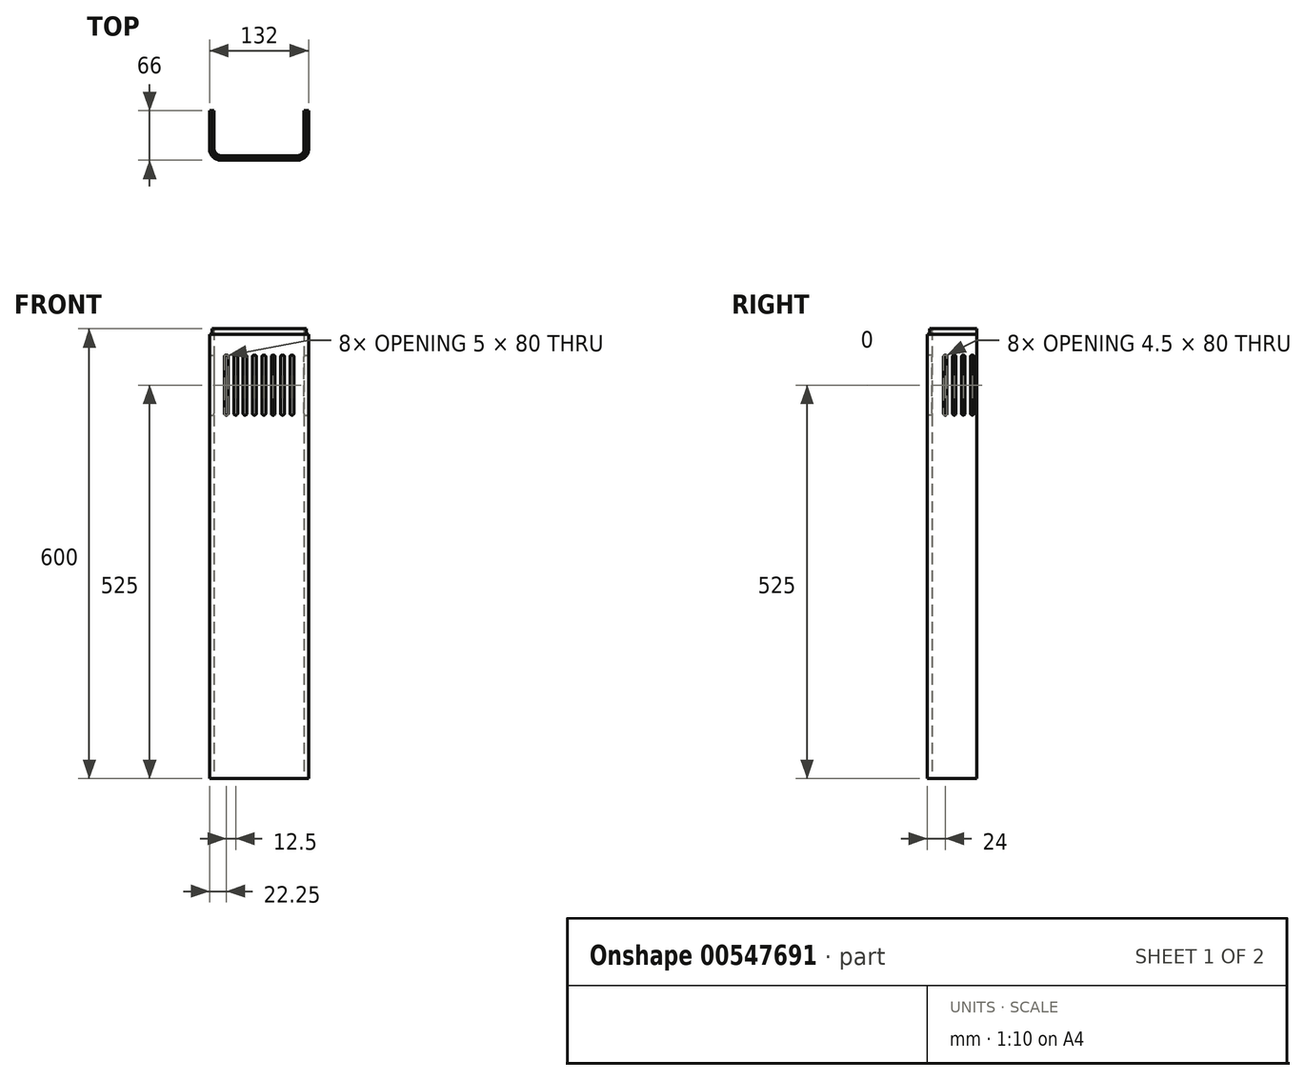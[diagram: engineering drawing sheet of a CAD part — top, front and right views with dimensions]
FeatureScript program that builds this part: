
annotation { "Feature Type Name" : "Feature", "Feature Type Description" : "" }
export const myFeature = defineFeature(function(context is Context, id is Id, definition is map)
    precondition{}
    {
        {
            var Q0;
            Q0=qCreatedBy(makeId("Top.planeOp"),FACE);
            var sketch = newSketch(context, id + "F0", { "sketchPlane" : qUnion([Q0])});
            skLineSegment(sketch, "E0", {"start": v(-66, 0) * mm, "end": v(-66, -51) * mm});
            skLineSegment(sketch, "E1", {"start": v(-51, -66) * mm, "end": v(51, -66) * mm});
            skLineSegment(sketch, "E2", {"start": v(66, -51) * mm, "end": v(66, 0) * mm});
            skPoint(sketch, "E3", {"position": v(0, -66) * mm});
            skPoint(sketch, "E4.visualSharp", {"position": v(-66, -66) * mm});
            skArc(sketch, "E4.filletArc", {"start": v(-66, -51) * mm, "mid": v(-61.6, -61.6) * mm, "end": v(-51, -66) * mm});
            skPoint(sketch, "E5.visualSharp", {"position": v(66, -66) * mm});
            skArc(sketch, "E5.filletArc", {"start": v(51, -66) * mm, "mid": v(61.6, -61.6) * mm, "end": v(66, -51) * mm});
            skLineSegment(sketch, "E6.0", {"start": v(-60, 0) * mm, "end": v(-60, -51) * mm});
            skArc(sketch, "E7.0", {"start": v(-60, -51) * mm, "mid": v(-57.36, -57.36) * mm, "end": v(-51, -60) * mm});
            skLineSegment(sketch, "E8.0", {"start": v(60, -51) * mm, "end": v(60, 0) * mm});
            skArc(sketch, "E8.1", {"start": v(51, -60) * mm, "mid": v(57.36, -57.36) * mm, "end": v(60, -51) * mm});
            skLineSegment(sketch, "E8.2", {"start": v(-51, -60) * mm, "end": v(51, -60) * mm});
            skLineSegment(sketch, "E9", {"start": v(-66, 0) * mm, "end": v(-60, 0) * mm});
            skLineSegment(sketch, "E10", {"start": v(60, 0) * mm, "end": v(66, 0) * mm});
            skSolve(sketch);
        }
        {
            var Q0;
            Q0 = qSketchRegion(id + "F0", true);
            extrude(context, id + "F1", {"entities" : qUnion([Q0]), "depth" : 600 * mm, "offsetDistance" : 25 * mm});
        }
        {
            var Q0;
            Q0=makeQuery(id+"F1.opExtrude","SWEPT_FACE",FACE,{"disambiguationData":[OSD([sQuery(id+"F0.wireOp",EDGE,"E1")])]});
            var sketch = newSketch(context, id + "F2", { "sketchPlane" : qUnion([Q0])});
            skLineSegment(sketch, "E11.bottom", {"start": v(-46.25, 565) * mm, "end": v(-41.25, 565) * mm});
            skLineSegment(sketch, "E11.top", {"start": v(-46.25, 485) * mm, "end": v(-41.25, 485) * mm});
            skLineSegment(sketch, "E11.left", {"start": v(-46.25, 565) * mm, "end": v(-46.25, 485) * mm});
            skLineSegment(sketch, "E11.right", {"start": v(-41.25, 565) * mm, "end": v(-41.25, 485) * mm});
            skLineSegment(sketch, "E12", {"start": v(-41.25, 565) * mm, "end": v(-33.75, 565) * mm, "construction": true});
            skPoint(sketch, "E13", {"position": v(0, 600) * mm});
            skLineSegment(sketch, "E14.bottom", {"start": v(-33.75, 565) * mm, "end": v(-28.75, 565) * mm});
            skLineSegment(sketch, "E14.top", {"start": v(-33.75, 485) * mm, "end": v(-28.75, 485) * mm});
            skLineSegment(sketch, "E14.left", {"start": v(-33.75, 565) * mm, "end": v(-33.75, 485) * mm});
            skLineSegment(sketch, "E14.right", {"start": v(-28.75, 565) * mm, "end": v(-28.75, 485) * mm});
            skLineSegment(sketch, "E15.bottom", {"start": v(-21.25, 565) * mm, "end": v(-16.25, 565) * mm});
            skLineSegment(sketch, "E15.top", {"start": v(-21.25, 485) * mm, "end": v(-16.25, 485) * mm});
            skLineSegment(sketch, "E15.left", {"start": v(-21.25, 565) * mm, "end": v(-21.25, 485) * mm});
            skLineSegment(sketch, "E15.right", {"start": v(-16.25, 565) * mm, "end": v(-16.25, 485) * mm});
            skLineSegment(sketch, "E16.bottom", {"start": v(-8.75, 565) * mm, "end": v(-3.75, 565) * mm});
            skLineSegment(sketch, "E16.top", {"start": v(-8.75, 485) * mm, "end": v(-3.75, 485) * mm});
            skLineSegment(sketch, "E16.left", {"start": v(-8.75, 565) * mm, "end": v(-8.75, 485) * mm});
            skLineSegment(sketch, "E16.right", {"start": v(-3.75, 565) * mm, "end": v(-3.75, 485) * mm});
            skLineSegment(sketch, "E17.bottom", {"start": v(3.75, 565) * mm, "end": v(8.75, 565) * mm});
            skLineSegment(sketch, "E17.top", {"start": v(3.75, 485) * mm, "end": v(8.75, 485) * mm});
            skLineSegment(sketch, "E17.left", {"start": v(3.75, 565) * mm, "end": v(3.75, 485) * mm});
            skLineSegment(sketch, "E17.right", {"start": v(8.75, 565) * mm, "end": v(8.75, 485) * mm});
            skLineSegment(sketch, "E18.bottom", {"start": v(16.25, 565) * mm, "end": v(21.25, 565) * mm});
            skLineSegment(sketch, "E18.top", {"start": v(16.25, 485) * mm, "end": v(21.25, 485) * mm});
            skLineSegment(sketch, "E18.left", {"start": v(16.25, 565) * mm, "end": v(16.25, 485) * mm});
            skLineSegment(sketch, "E18.right", {"start": v(21.25, 565) * mm, "end": v(21.25, 485) * mm});
            skLineSegment(sketch, "E19.bottom", {"start": v(28.75, 565) * mm, "end": v(33.75, 565) * mm});
            skLineSegment(sketch, "E19.top", {"start": v(28.75, 485) * mm, "end": v(33.75, 485) * mm});
            skLineSegment(sketch, "E19.left", {"start": v(28.75, 565) * mm, "end": v(28.75, 485) * mm});
            skLineSegment(sketch, "E19.right", {"start": v(33.75, 565) * mm, "end": v(33.75, 485) * mm});
            skLineSegment(sketch, "E20.bottom", {"start": v(41.25, 565) * mm, "end": v(46.25, 565) * mm});
            skLineSegment(sketch, "E20.top", {"start": v(41.25, 485) * mm, "end": v(46.25, 485) * mm});
            skLineSegment(sketch, "E20.left", {"start": v(41.25, 565) * mm, "end": v(41.25, 485) * mm});
            skLineSegment(sketch, "E20.right", {"start": v(46.25, 565) * mm, "end": v(46.25, 485) * mm});
            skLineSegment(sketch, "E21", {"start": v(-28.75, 565) * mm, "end": v(-21.25, 565) * mm, "construction": true});
            skLineSegment(sketch, "E22", {"start": v(-16.25, 565) * mm, "end": v(-8.75, 565) * mm, "construction": true});
            skLineSegment(sketch, "E23", {"start": v(-3.75, 565) * mm, "end": v(3.75, 565) * mm, "construction": true});
            skLineSegment(sketch, "E24", {"start": v(8.75, 565) * mm, "end": v(16.25, 565) * mm, "construction": true});
            skLineSegment(sketch, "E25", {"start": v(21.25, 565) * mm, "end": v(28.75, 565) * mm, "construction": true});
            skLineSegment(sketch, "E26", {"start": v(33.75, 565) * mm, "end": v(41.25, 565) * mm, "construction": true});
            skPoint(sketch, "E27", {"position": v(0, 565) * mm});
            skSolve(sketch);
        }
        {
            var Q0;
            Q0=makeQuery(id+"F2.imprint","IMPRINT",FACE,{"disambiguationData":[TD([[makeQuery(id+"F2.imprint","IMPRINT",EDGE,{"derivedFrom":sQuery(id+"F2.wireOp",EDGE,"E11.bottom")}),-1.0]])]});
            var Q1;
            Q1=makeQuery(id+"F2.imprint","IMPRINT",FACE,{"disambiguationData":[TD([[makeQuery(id+"F2.imprint","IMPRINT",EDGE,{"derivedFrom":sQuery(id+"F2.wireOp",EDGE,"E14.bottom")}),-1.0]])]});
            var Q2;
            Q2=makeQuery(id+"F2.imprint","IMPRINT",FACE,{"disambiguationData":[TD([[makeQuery(id+"F2.imprint","IMPRINT",EDGE,{"derivedFrom":sQuery(id+"F2.wireOp",EDGE,"E15.bottom")}),-1.0]])]});
            var Q3;
            Q3=makeQuery(id+"F2.imprint","IMPRINT",FACE,{"disambiguationData":[TD([[makeQuery(id+"F2.imprint","IMPRINT",EDGE,{"derivedFrom":sQuery(id+"F2.wireOp",EDGE,"E16.bottom")}),-1.0]])]});
            var Q4;
            Q4=makeQuery(id+"F2.imprint","IMPRINT",FACE,{"disambiguationData":[TD([[makeQuery(id+"F2.imprint","IMPRINT",EDGE,{"derivedFrom":sQuery(id+"F2.wireOp",EDGE,"E17.bottom")}),-1.0]])]});
            var Q5;
            Q5=makeQuery(id+"F2.imprint","IMPRINT",FACE,{"disambiguationData":[TD([[makeQuery(id+"F2.imprint","IMPRINT",EDGE,{"derivedFrom":sQuery(id+"F2.wireOp",EDGE,"E18.bottom")}),-1.0]])]});
            var Q6;
            Q6=makeQuery(id+"F2.imprint","IMPRINT",FACE,{"disambiguationData":[TD([[makeQuery(id+"F2.imprint","IMPRINT",EDGE,{"derivedFrom":sQuery(id+"F2.wireOp",EDGE,"E19.bottom")}),-1.0]])]});
            var Q7;
            Q7=makeQuery(id+"F2.imprint","IMPRINT",FACE,{"disambiguationData":[TD([[makeQuery(id+"F2.imprint","IMPRINT",EDGE,{"derivedFrom":sQuery(id+"F2.wireOp",EDGE,"E20.bottom")}),-1.0]])]});
            extrude(context, id + "F3", {"entities" : qUnion([Q0, Q1, Q2, Q3, Q4, Q5, Q6, Q7]), "operationType" : NewBodyOperationType.REMOVE, "oppositeDirection" : true, "depth" : 25 * mm, "offsetDistance" : 25 * mm});
        }
        {
            var Q0;
            Q0=makeQuery(id+"F3.boolean.opBoolean","COPY",EDGE,{"derivedFrom":makeQuery(id+"F3.opExtrude","SWEPT_EDGE",EDGE,{"disambiguationData":[OSD([sQuery(id+"F2.wireOp",EDGE,"E11.top"),sQuery(id+"F2.wireOp",EDGE,"E11.left")])]})});
            var Q1;
            Q1=makeQuery(id+"F3.boolean.opBoolean","COPY",EDGE,{"derivedFrom":makeQuery(id+"F3.opExtrude","SWEPT_EDGE",EDGE,{"disambiguationData":[OSD([sQuery(id+"F2.wireOp",EDGE,"E14.top"),sQuery(id+"F2.wireOp",EDGE,"E14.left")])]})});
            var Q2;
            Q2=makeQuery(id+"F3.boolean.opBoolean","COPY",EDGE,{"derivedFrom":makeQuery(id+"F3.opExtrude","SWEPT_EDGE",EDGE,{"disambiguationData":[OSD([sQuery(id+"F2.wireOp",EDGE,"E15.top"),sQuery(id+"F2.wireOp",EDGE,"E15.left")])]})});
            var Q3;
            Q3=makeQuery(id+"F3.boolean.opBoolean","COPY",EDGE,{"derivedFrom":makeQuery(id+"F3.opExtrude","SWEPT_EDGE",EDGE,{"disambiguationData":[OSD([sQuery(id+"F2.wireOp",EDGE,"E16.top"),sQuery(id+"F2.wireOp",EDGE,"E16.left")])]})});
            var Q4;
            Q4=makeQuery(id+"F3.boolean.opBoolean","COPY",EDGE,{"derivedFrom":makeQuery(id+"F3.opExtrude","SWEPT_EDGE",EDGE,{"disambiguationData":[OSD([sQuery(id+"F2.wireOp",EDGE,"E17.top"),sQuery(id+"F2.wireOp",EDGE,"E17.left")])]})});
            var Q5;
            Q5=makeQuery(id+"F3.boolean.opBoolean","COPY",EDGE,{"derivedFrom":makeQuery(id+"F3.opExtrude","SWEPT_EDGE",EDGE,{"disambiguationData":[OSD([sQuery(id+"F2.wireOp",EDGE,"E18.top"),sQuery(id+"F2.wireOp",EDGE,"E18.left")])]})});
            var Q6;
            Q6=makeQuery(id+"F3.boolean.opBoolean","COPY",EDGE,{"derivedFrom":makeQuery(id+"F3.opExtrude","SWEPT_EDGE",EDGE,{"disambiguationData":[OSD([sQuery(id+"F2.wireOp",EDGE,"E19.top"),sQuery(id+"F2.wireOp",EDGE,"E19.left")])]})});
            var Q7;
            Q7=makeQuery(id+"F3.boolean.opBoolean","COPY",EDGE,{"derivedFrom":makeQuery(id+"F3.opExtrude","SWEPT_EDGE",EDGE,{"disambiguationData":[OSD([sQuery(id+"F2.wireOp",EDGE,"E20.top"),sQuery(id+"F2.wireOp",EDGE,"E20.left")])]})});
            var Q8;
            Q8=makeQuery(id+"F3.boolean.opBoolean","COPY",EDGE,{"derivedFrom":makeQuery(id+"F3.opExtrude","SWEPT_EDGE",EDGE,{"disambiguationData":[OSD([sQuery(id+"F2.wireOp",EDGE,"E11.bottom"),sQuery(id+"F2.wireOp",EDGE,"E11.left")])]})});
            var Q9;
            Q9=makeQuery(id+"F3.boolean.opBoolean","COPY",EDGE,{"derivedFrom":makeQuery(id+"F3.opExtrude","SWEPT_EDGE",EDGE,{"disambiguationData":[OSD([sQuery(id+"F2.wireOp",EDGE,"E14.bottom"),sQuery(id+"F2.wireOp",EDGE,"E14.left")])]})});
            var Q10;
            Q10=makeQuery(id+"F3.boolean.opBoolean","COPY",EDGE,{"derivedFrom":makeQuery(id+"F3.opExtrude","SWEPT_EDGE",EDGE,{"disambiguationData":[OSD([sQuery(id+"F2.wireOp",EDGE,"E15.bottom"),sQuery(id+"F2.wireOp",EDGE,"E15.left")])]})});
            var Q11;
            Q11=makeQuery(id+"F3.boolean.opBoolean","COPY",EDGE,{"derivedFrom":makeQuery(id+"F3.opExtrude","SWEPT_EDGE",EDGE,{"disambiguationData":[OSD([sQuery(id+"F2.wireOp",EDGE,"E16.bottom"),sQuery(id+"F2.wireOp",EDGE,"E16.left")])]})});
            var Q12;
            Q12=makeQuery(id+"F3.boolean.opBoolean","COPY",EDGE,{"derivedFrom":makeQuery(id+"F3.opExtrude","SWEPT_EDGE",EDGE,{"disambiguationData":[OSD([sQuery(id+"F2.wireOp",EDGE,"E17.bottom"),sQuery(id+"F2.wireOp",EDGE,"E17.left")])]})});
            var Q13;
            Q13=makeQuery(id+"F3.boolean.opBoolean","COPY",EDGE,{"derivedFrom":makeQuery(id+"F3.opExtrude","SWEPT_EDGE",EDGE,{"disambiguationData":[OSD([sQuery(id+"F2.wireOp",EDGE,"E18.bottom"),sQuery(id+"F2.wireOp",EDGE,"E18.left")])]})});
            var Q14;
            Q14=makeQuery(id+"F3.boolean.opBoolean","COPY",EDGE,{"derivedFrom":makeQuery(id+"F3.opExtrude","SWEPT_EDGE",EDGE,{"disambiguationData":[OSD([sQuery(id+"F2.wireOp",EDGE,"E19.bottom"),sQuery(id+"F2.wireOp",EDGE,"E19.left")])]})});
            var Q15;
            Q15=makeQuery(id+"F3.boolean.opBoolean","COPY",EDGE,{"derivedFrom":makeQuery(id+"F3.opExtrude","SWEPT_EDGE",EDGE,{"disambiguationData":[OSD([sQuery(id+"F2.wireOp",EDGE,"E20.bottom"),sQuery(id+"F2.wireOp",EDGE,"E20.left")])]})});
            var Q16;
            Q16=makeQuery(id+"F3.boolean.opBoolean","COPY",EDGE,{"derivedFrom":makeQuery(id+"F3.opExtrude","SWEPT_EDGE",EDGE,{"disambiguationData":[OSD([sQuery(id+"F2.wireOp",EDGE,"E11.bottom"),sQuery(id+"F2.wireOp",EDGE,"E11.right")])]})});
            var Q17;
            Q17=makeQuery(id+"F3.boolean.opBoolean","COPY",EDGE,{"derivedFrom":makeQuery(id+"F3.opExtrude","SWEPT_EDGE",EDGE,{"disambiguationData":[OSD([sQuery(id+"F2.wireOp",EDGE,"E14.bottom"),sQuery(id+"F2.wireOp",EDGE,"E14.right")])]})});
            var Q18;
            Q18=makeQuery(id+"F3.boolean.opBoolean","COPY",EDGE,{"derivedFrom":makeQuery(id+"F3.opExtrude","SWEPT_EDGE",EDGE,{"disambiguationData":[OSD([sQuery(id+"F2.wireOp",EDGE,"E15.bottom"),sQuery(id+"F2.wireOp",EDGE,"E15.right")])]})});
            var Q19;
            Q19=makeQuery(id+"F3.boolean.opBoolean","COPY",EDGE,{"derivedFrom":makeQuery(id+"F3.opExtrude","SWEPT_EDGE",EDGE,{"disambiguationData":[OSD([sQuery(id+"F2.wireOp",EDGE,"E16.bottom"),sQuery(id+"F2.wireOp",EDGE,"E16.right")])]})});
            var Q20;
            Q20=makeQuery(id+"F3.boolean.opBoolean","COPY",EDGE,{"derivedFrom":makeQuery(id+"F3.opExtrude","SWEPT_EDGE",EDGE,{"disambiguationData":[OSD([sQuery(id+"F2.wireOp",EDGE,"E17.bottom"),sQuery(id+"F2.wireOp",EDGE,"E17.right")])]})});
            var Q21;
            Q21=makeQuery(id+"F3.boolean.opBoolean","COPY",EDGE,{"derivedFrom":makeQuery(id+"F3.opExtrude","SWEPT_EDGE",EDGE,{"disambiguationData":[OSD([sQuery(id+"F2.wireOp",EDGE,"E18.bottom"),sQuery(id+"F2.wireOp",EDGE,"E18.right")])]})});
            var Q22;
            Q22=makeQuery(id+"F3.boolean.opBoolean","COPY",EDGE,{"derivedFrom":makeQuery(id+"F3.opExtrude","SWEPT_EDGE",EDGE,{"disambiguationData":[OSD([sQuery(id+"F2.wireOp",EDGE,"E19.bottom"),sQuery(id+"F2.wireOp",EDGE,"E19.right")])]})});
            var Q23;
            Q23=makeQuery(id+"F3.boolean.opBoolean","COPY",EDGE,{"derivedFrom":makeQuery(id+"F3.opExtrude","SWEPT_EDGE",EDGE,{"disambiguationData":[OSD([sQuery(id+"F2.wireOp",EDGE,"E20.bottom"),sQuery(id+"F2.wireOp",EDGE,"E20.right")])]})});
            var Q24;
            Q24=makeQuery(id+"F3.boolean.opBoolean","COPY",EDGE,{"derivedFrom":makeQuery(id+"F3.opExtrude","SWEPT_EDGE",EDGE,{"disambiguationData":[OSD([sQuery(id+"F2.wireOp",EDGE,"E20.top"),sQuery(id+"F2.wireOp",EDGE,"E20.right")])]})});
            var Q25;
            Q25=makeQuery(id+"F3.boolean.opBoolean","COPY",EDGE,{"derivedFrom":makeQuery(id+"F3.opExtrude","SWEPT_EDGE",EDGE,{"disambiguationData":[OSD([sQuery(id+"F2.wireOp",EDGE,"E19.top"),sQuery(id+"F2.wireOp",EDGE,"E19.right")])]})});
            var Q26;
            Q26=makeQuery(id+"F3.boolean.opBoolean","COPY",EDGE,{"derivedFrom":makeQuery(id+"F3.opExtrude","SWEPT_EDGE",EDGE,{"disambiguationData":[OSD([sQuery(id+"F2.wireOp",EDGE,"E18.top"),sQuery(id+"F2.wireOp",EDGE,"E18.right")])]})});
            var Q27;
            Q27=makeQuery(id+"F3.boolean.opBoolean","COPY",EDGE,{"derivedFrom":makeQuery(id+"F3.opExtrude","SWEPT_EDGE",EDGE,{"disambiguationData":[OSD([sQuery(id+"F2.wireOp",EDGE,"E17.top"),sQuery(id+"F2.wireOp",EDGE,"E17.right")])]})});
            var Q28;
            Q28=makeQuery(id+"F3.boolean.opBoolean","COPY",EDGE,{"derivedFrom":makeQuery(id+"F3.opExtrude","SWEPT_EDGE",EDGE,{"disambiguationData":[OSD([sQuery(id+"F2.wireOp",EDGE,"E16.top"),sQuery(id+"F2.wireOp",EDGE,"E16.right")])]})});
            var Q29;
            Q29=makeQuery(id+"F3.boolean.opBoolean","COPY",EDGE,{"derivedFrom":makeQuery(id+"F3.opExtrude","SWEPT_EDGE",EDGE,{"disambiguationData":[OSD([sQuery(id+"F2.wireOp",EDGE,"E15.top"),sQuery(id+"F2.wireOp",EDGE,"E15.right")])]})});
            var Q30;
            Q30=makeQuery(id+"F3.boolean.opBoolean","COPY",EDGE,{"derivedFrom":makeQuery(id+"F3.opExtrude","SWEPT_EDGE",EDGE,{"disambiguationData":[OSD([sQuery(id+"F2.wireOp",EDGE,"E14.top"),sQuery(id+"F2.wireOp",EDGE,"E14.right")])]})});
            var Q31;
            Q31=makeQuery(id+"F3.boolean.opBoolean","COPY",EDGE,{"derivedFrom":makeQuery(id+"F3.opExtrude","SWEPT_EDGE",EDGE,{"disambiguationData":[OSD([sQuery(id+"F2.wireOp",EDGE,"E11.top"),sQuery(id+"F2.wireOp",EDGE,"E11.right")])]})});
            fillet(context, id + "F4", {"entities" : qUnion([Q0, Q1, Q2, Q3, Q4, Q5, Q6, Q7, Q8, Q9, Q10, Q11, Q12, Q13, Q14, Q15, Q16, Q17, Q18, Q19, Q20, Q21, Q22, Q23, Q24, Q25, Q26, Q27, Q28, Q29, Q30, Q31]), "radius" : 2 * mm, "tangentPropagation" : true, "allowEdgeOverflow" : false});
        }
        {
            var Q0;
            Q0=makeQuery(id+"F1.opExtrude","SWEPT_FACE",FACE,{"disambiguationData":[OSD([sQuery(id+"F0.wireOp",EDGE,"E2")])]});
            var sketch = newSketch(context, id + "F5", { "sketchPlane" : qUnion([Q0])});
            skLineSegment(sketch, "E28.bottom", {"start": v(-44.25, 485) * mm, "end": v(-39.75, 485) * mm});
            skLineSegment(sketch, "E28.top", {"start": v(-44.25, 565) * mm, "end": v(-39.75, 565) * mm});
            skLineSegment(sketch, "E28.left", {"start": v(-44.25, 485) * mm, "end": v(-44.25, 565) * mm});
            skLineSegment(sketch, "E28.right", {"start": v(-39.75, 485) * mm, "end": v(-39.75, 565) * mm});
            skLineSegment(sketch, "E29.bottom", {"start": v(-32.25, 565) * mm, "end": v(-27.75, 565) * mm});
            skLineSegment(sketch, "E29.top", {"start": v(-32.25, 485) * mm, "end": v(-27.75, 485) * mm});
            skLineSegment(sketch, "E29.left", {"start": v(-32.25, 565) * mm, "end": v(-32.25, 485) * mm});
            skLineSegment(sketch, "E29.right", {"start": v(-27.75, 565) * mm, "end": v(-27.75, 485) * mm});
            skLineSegment(sketch, "E30.bottom", {"start": v(-20.25, 565) * mm, "end": v(-15.75, 565) * mm});
            skLineSegment(sketch, "E30.top", {"start": v(-20.25, 485) * mm, "end": v(-15.75, 485) * mm});
            skLineSegment(sketch, "E30.left", {"start": v(-20.25, 565) * mm, "end": v(-20.25, 485) * mm});
            skLineSegment(sketch, "E30.right", {"start": v(-15.75, 565) * mm, "end": v(-15.75, 485) * mm});
            skLineSegment(sketch, "E31.bottom", {"start": v(-8.25, 565) * mm, "end": v(-3.75, 565) * mm});
            skLineSegment(sketch, "E31.top", {"start": v(-8.25, 485) * mm, "end": v(-3.75, 485) * mm});
            skLineSegment(sketch, "E31.left", {"start": v(-8.25, 565) * mm, "end": v(-8.25, 485) * mm});
            skLineSegment(sketch, "E31.right", {"start": v(-3.75, 565) * mm, "end": v(-3.75, 485) * mm});
            skLineSegment(sketch, "E32", {"start": v(-39.75, 565) * mm, "end": v(-32.25, 565) * mm, "construction": true});
            skLineSegment(sketch, "E33", {"start": v(-27.75, 565) * mm, "end": v(-20.25, 565) * mm, "construction": true});
            skLineSegment(sketch, "E34", {"start": v(-15.75, 565) * mm, "end": v(-8.25, 565) * mm, "construction": true});
            skLineSegment(sketch, "E35", {"start": v(-3.75, 565) * mm, "end": v(3.75, 565) * mm, "construction": true});
            skPoint(sketch, "E36", {"position": v(0, 565) * mm});
            skSolve(sketch);
        }
        {
            var Q0;
            Q0=makeQuery(id+"F5.imprint","IMPRINT",FACE,{"disambiguationData":[TD([[makeQuery(id+"F5.imprint","IMPRINT",EDGE,{"derivedFrom":sQuery(id+"F5.wireOp",EDGE,"E28.bottom")}),1.0]])]});
            var Q1;
            Q1=makeQuery(id+"F5.imprint","IMPRINT",FACE,{"disambiguationData":[TD([[makeQuery(id+"F5.imprint","IMPRINT",EDGE,{"derivedFrom":sQuery(id+"F5.wireOp",EDGE,"E29.bottom")}),-1.0]])]});
            var Q2;
            Q2=makeQuery(id+"F5.imprint","IMPRINT",FACE,{"disambiguationData":[TD([[makeQuery(id+"F5.imprint","IMPRINT",EDGE,{"derivedFrom":sQuery(id+"F5.wireOp",EDGE,"E30.bottom")}),-1.0]])]});
            var Q3;
            Q3=makeQuery(id+"F5.imprint","IMPRINT",FACE,{"disambiguationData":[TD([[makeQuery(id+"F5.imprint","IMPRINT",EDGE,{"derivedFrom":sQuery(id+"F5.wireOp",EDGE,"E31.bottom")}),-1.0]])]});
            extrude(context, id + "F6", {"entities" : qUnion([Q0, Q1, Q2, Q3]), "operationType" : NewBodyOperationType.REMOVE, "endBound" : BoundingType.THROUGH_ALL, "oppositeDirection" : true, "depth" : 25 * mm, "offsetDistance" : 25 * mm});
        }
        {
            var Q0;
            {var subQ0=sQuery(id+"F5.wireOp",EDGE,"E31.top");var subQ1=sQuery(id+"F5.wireOp",EDGE,"E31.right");Q0=makeQuery(id+"F6.boolean.opBoolean","COPY",EDGE,{"disambiguationData":[TD([makeQuery(id+"F1.opExtrude","SWEPT_FACE",FACE,{"disambiguationData":[OSD([sQuery(id+"F0.wireOp",EDGE,"E2")])]})])],"derivedFrom":makeQuery(id+"F6.opExtrude","SWEPT_EDGE",EDGE,{"disambiguationData":[OSD([subQ0,subQ1])]})});}
            var Q1;
            {var subQ0=sQuery(id+"F5.wireOp",EDGE,"E30.top");var subQ1=sQuery(id+"F5.wireOp",EDGE,"E30.right");Q1=makeQuery(id+"F6.boolean.opBoolean","COPY",EDGE,{"disambiguationData":[TD([makeQuery(id+"F1.opExtrude","SWEPT_FACE",FACE,{"disambiguationData":[OSD([sQuery(id+"F0.wireOp",EDGE,"E2")])]})])],"derivedFrom":makeQuery(id+"F6.opExtrude","SWEPT_EDGE",EDGE,{"disambiguationData":[OSD([subQ0,subQ1])]})});}
            var Q2;
            {var subQ0=sQuery(id+"F5.wireOp",EDGE,"E29.right");var subQ1=sQuery(id+"F5.wireOp",EDGE,"E29.top");Q2=makeQuery(id+"F6.boolean.opBoolean","COPY",EDGE,{"disambiguationData":[TD([makeQuery(id+"F1.opExtrude","SWEPT_FACE",FACE,{"disambiguationData":[OSD([sQuery(id+"F0.wireOp",EDGE,"E2")])]})])],"derivedFrom":makeQuery(id+"F6.opExtrude","SWEPT_EDGE",EDGE,{"disambiguationData":[OSD([subQ1,subQ0])]})});}
            var Q3;
            {var subQ0=sQuery(id+"F5.wireOp",EDGE,"E28.bottom");var subQ1=sQuery(id+"F5.wireOp",EDGE,"E28.right");Q3=makeQuery(id+"F6.boolean.opBoolean","COPY",EDGE,{"disambiguationData":[TD([makeQuery(id+"F1.opExtrude","SWEPT_FACE",FACE,{"disambiguationData":[OSD([sQuery(id+"F0.wireOp",EDGE,"E2")])]})])],"derivedFrom":makeQuery(id+"F6.opExtrude","SWEPT_EDGE",EDGE,{"disambiguationData":[OSD([subQ0,subQ1])]})});}
            var Q4;
            {var subQ0=sQuery(id+"F5.wireOp",EDGE,"E28.bottom");var subQ1=sQuery(id+"F5.wireOp",EDGE,"E28.left");Q4=makeQuery(id+"F6.boolean.opBoolean","COPY",EDGE,{"disambiguationData":[TD([makeQuery(id+"F1.opExtrude","SWEPT_FACE",FACE,{"disambiguationData":[OSD([sQuery(id+"F0.wireOp",EDGE,"E2")])]})])],"derivedFrom":makeQuery(id+"F6.opExtrude","SWEPT_EDGE",EDGE,{"disambiguationData":[OSD([subQ0,subQ1])]})});}
            var Q5;
            {var subQ0=sQuery(id+"F5.wireOp",EDGE,"E29.top");var subQ1=sQuery(id+"F5.wireOp",EDGE,"E29.left");Q5=makeQuery(id+"F6.boolean.opBoolean","COPY",EDGE,{"disambiguationData":[TD([makeQuery(id+"F1.opExtrude","SWEPT_FACE",FACE,{"disambiguationData":[OSD([sQuery(id+"F0.wireOp",EDGE,"E2")])]})])],"derivedFrom":makeQuery(id+"F6.opExtrude","SWEPT_EDGE",EDGE,{"disambiguationData":[OSD([subQ0,subQ1])]})});}
            var Q6;
            {var subQ0=sQuery(id+"F5.wireOp",EDGE,"E30.left");var subQ1=sQuery(id+"F5.wireOp",EDGE,"E30.top");Q6=makeQuery(id+"F6.boolean.opBoolean","COPY",EDGE,{"disambiguationData":[TD([makeQuery(id+"F1.opExtrude","SWEPT_FACE",FACE,{"disambiguationData":[OSD([sQuery(id+"F0.wireOp",EDGE,"E2")])]})])],"derivedFrom":makeQuery(id+"F6.opExtrude","SWEPT_EDGE",EDGE,{"disambiguationData":[OSD([subQ1,subQ0])]})});}
            var Q7;
            {var subQ0=sQuery(id+"F5.wireOp",EDGE,"E31.top");var subQ1=sQuery(id+"F5.wireOp",EDGE,"E31.left");Q7=makeQuery(id+"F6.boolean.opBoolean","COPY",EDGE,{"disambiguationData":[TD([makeQuery(id+"F1.opExtrude","SWEPT_FACE",FACE,{"disambiguationData":[OSD([sQuery(id+"F0.wireOp",EDGE,"E2")])]})])],"derivedFrom":makeQuery(id+"F6.opExtrude","SWEPT_EDGE",EDGE,{"disambiguationData":[OSD([subQ0,subQ1])]})});}
            var Q8;
            {var subQ0=sQuery(id+"F5.wireOp",EDGE,"E28.top");var subQ1=sQuery(id+"F5.wireOp",EDGE,"E28.right");Q8=makeQuery(id+"F6.boolean.opBoolean","COPY",EDGE,{"disambiguationData":[TD([makeQuery(id+"F1.opExtrude","SWEPT_FACE",FACE,{"disambiguationData":[OSD([sQuery(id+"F0.wireOp",EDGE,"E2")])]})])],"derivedFrom":makeQuery(id+"F6.opExtrude","SWEPT_EDGE",EDGE,{"disambiguationData":[OSD([subQ0,subQ1])]})});}
            var Q9;
            {var subQ0=sQuery(id+"F5.wireOp",EDGE,"E29.bottom");var subQ1=sQuery(id+"F5.wireOp",EDGE,"E29.right");Q9=makeQuery(id+"F6.boolean.opBoolean","COPY",EDGE,{"disambiguationData":[TD([makeQuery(id+"F1.opExtrude","SWEPT_FACE",FACE,{"disambiguationData":[OSD([sQuery(id+"F0.wireOp",EDGE,"E2")])]})])],"derivedFrom":makeQuery(id+"F6.opExtrude","SWEPT_EDGE",EDGE,{"disambiguationData":[OSD([subQ0,subQ1])]})});}
            var Q10;
            {var subQ0=sQuery(id+"F5.wireOp",EDGE,"E30.bottom");var subQ1=sQuery(id+"F5.wireOp",EDGE,"E30.right");Q10=makeQuery(id+"F6.boolean.opBoolean","COPY",EDGE,{"disambiguationData":[TD([makeQuery(id+"F1.opExtrude","SWEPT_FACE",FACE,{"disambiguationData":[OSD([sQuery(id+"F0.wireOp",EDGE,"E2")])]})])],"derivedFrom":makeQuery(id+"F6.opExtrude","SWEPT_EDGE",EDGE,{"disambiguationData":[OSD([subQ0,subQ1])]})});}
            var Q11;
            {var subQ0=sQuery(id+"F5.wireOp",EDGE,"E31.bottom");var subQ1=sQuery(id+"F5.wireOp",EDGE,"E31.right");Q11=makeQuery(id+"F6.boolean.opBoolean","COPY",EDGE,{"disambiguationData":[TD([makeQuery(id+"F1.opExtrude","SWEPT_FACE",FACE,{"disambiguationData":[OSD([sQuery(id+"F0.wireOp",EDGE,"E2")])]})])],"derivedFrom":makeQuery(id+"F6.opExtrude","SWEPT_EDGE",EDGE,{"disambiguationData":[OSD([subQ0,subQ1])]})});}
            var Q12;
            {var subQ0=sQuery(id+"F5.wireOp",EDGE,"E31.bottom");var subQ1=sQuery(id+"F5.wireOp",EDGE,"E31.left");Q12=makeQuery(id+"F6.boolean.opBoolean","COPY",EDGE,{"disambiguationData":[TD([makeQuery(id+"F1.opExtrude","SWEPT_FACE",FACE,{"disambiguationData":[OSD([sQuery(id+"F0.wireOp",EDGE,"E2")])]})])],"derivedFrom":makeQuery(id+"F6.opExtrude","SWEPT_EDGE",EDGE,{"disambiguationData":[OSD([subQ0,subQ1])]})});}
            var Q13;
            {var subQ0=sQuery(id+"F5.wireOp",EDGE,"E30.left");var subQ1=sQuery(id+"F5.wireOp",EDGE,"E30.bottom");Q13=makeQuery(id+"F6.boolean.opBoolean","COPY",EDGE,{"disambiguationData":[TD([makeQuery(id+"F1.opExtrude","SWEPT_FACE",FACE,{"disambiguationData":[OSD([sQuery(id+"F0.wireOp",EDGE,"E2")])]})])],"derivedFrom":makeQuery(id+"F6.opExtrude","SWEPT_EDGE",EDGE,{"disambiguationData":[OSD([subQ1,subQ0])]})});}
            var Q14;
            {var subQ0=sQuery(id+"F5.wireOp",EDGE,"E29.bottom");var subQ1=sQuery(id+"F5.wireOp",EDGE,"E29.left");Q14=makeQuery(id+"F6.boolean.opBoolean","COPY",EDGE,{"disambiguationData":[TD([makeQuery(id+"F1.opExtrude","SWEPT_FACE",FACE,{"disambiguationData":[OSD([sQuery(id+"F0.wireOp",EDGE,"E2")])]})])],"derivedFrom":makeQuery(id+"F6.opExtrude","SWEPT_EDGE",EDGE,{"disambiguationData":[OSD([subQ0,subQ1])]})});}
            var Q15;
            {var subQ0=sQuery(id+"F5.wireOp",EDGE,"E28.top");var subQ1=sQuery(id+"F5.wireOp",EDGE,"E28.left");Q15=makeQuery(id+"F6.boolean.opBoolean","COPY",EDGE,{"disambiguationData":[TD([makeQuery(id+"F1.opExtrude","SWEPT_FACE",FACE,{"disambiguationData":[OSD([sQuery(id+"F0.wireOp",EDGE,"E2")])]})])],"derivedFrom":makeQuery(id+"F6.opExtrude","SWEPT_EDGE",EDGE,{"disambiguationData":[OSD([subQ0,subQ1])]})});}
            var Q16;
            {var subQ0=sQuery(id+"F5.wireOp",EDGE,"E28.left");var subQ1=sQuery(id+"F5.wireOp",EDGE,"E28.top");Q16=makeQuery(id+"F6.boolean.opBoolean","COPY",EDGE,{"disambiguationData":[TD([makeQuery(id+"F1.opExtrude","SWEPT_FACE",FACE,{"disambiguationData":[OSD([sQuery(id+"F0.wireOp",EDGE,"E0")])]})])],"derivedFrom":makeQuery(id+"F6.opExtrude","SWEPT_EDGE",EDGE,{"disambiguationData":[OSD([subQ1,subQ0])]})});}
            var Q17;
            {var subQ0=sQuery(id+"F5.wireOp",EDGE,"E29.bottom");var subQ1=sQuery(id+"F5.wireOp",EDGE,"E29.left");Q17=makeQuery(id+"F6.boolean.opBoolean","COPY",EDGE,{"disambiguationData":[TD([makeQuery(id+"F1.opExtrude","SWEPT_FACE",FACE,{"disambiguationData":[OSD([sQuery(id+"F0.wireOp",EDGE,"E0")])]})])],"derivedFrom":makeQuery(id+"F6.opExtrude","SWEPT_EDGE",EDGE,{"disambiguationData":[OSD([subQ0,subQ1])]})});}
            var Q18;
            {var subQ0=sQuery(id+"F5.wireOp",EDGE,"E30.bottom");var subQ1=sQuery(id+"F5.wireOp",EDGE,"E30.left");Q18=makeQuery(id+"F6.boolean.opBoolean","COPY",EDGE,{"disambiguationData":[TD([makeQuery(id+"F1.opExtrude","SWEPT_FACE",FACE,{"disambiguationData":[OSD([sQuery(id+"F0.wireOp",EDGE,"E0")])]})])],"derivedFrom":makeQuery(id+"F6.opExtrude","SWEPT_EDGE",EDGE,{"disambiguationData":[OSD([subQ0,subQ1])]})});}
            var Q19;
            {var subQ0=sQuery(id+"F5.wireOp",EDGE,"E31.left");var subQ1=sQuery(id+"F5.wireOp",EDGE,"E31.bottom");Q19=makeQuery(id+"F6.boolean.opBoolean","COPY",EDGE,{"disambiguationData":[TD([makeQuery(id+"F1.opExtrude","SWEPT_FACE",FACE,{"disambiguationData":[OSD([sQuery(id+"F0.wireOp",EDGE,"E0")])]})])],"derivedFrom":makeQuery(id+"F6.opExtrude","SWEPT_EDGE",EDGE,{"disambiguationData":[OSD([subQ1,subQ0])]})});}
            var Q20;
            {var subQ0=sQuery(id+"F5.wireOp",EDGE,"E28.left");var subQ1=sQuery(id+"F5.wireOp",EDGE,"E28.bottom");Q20=makeQuery(id+"F6.boolean.opBoolean","COPY",EDGE,{"disambiguationData":[TD([makeQuery(id+"F1.opExtrude","SWEPT_FACE",FACE,{"disambiguationData":[OSD([sQuery(id+"F0.wireOp",EDGE,"E0")])]})])],"derivedFrom":makeQuery(id+"F6.opExtrude","SWEPT_EDGE",EDGE,{"disambiguationData":[OSD([subQ1,subQ0])]})});}
            var Q21;
            {var subQ0=sQuery(id+"F5.wireOp",EDGE,"E29.top");var subQ1=sQuery(id+"F5.wireOp",EDGE,"E29.left");Q21=makeQuery(id+"F6.boolean.opBoolean","COPY",EDGE,{"disambiguationData":[TD([makeQuery(id+"F1.opExtrude","SWEPT_FACE",FACE,{"disambiguationData":[OSD([sQuery(id+"F0.wireOp",EDGE,"E0")])]})])],"derivedFrom":makeQuery(id+"F6.opExtrude","SWEPT_EDGE",EDGE,{"disambiguationData":[OSD([subQ0,subQ1])]})});}
            var Q22;
            {var subQ0=sQuery(id+"F5.wireOp",EDGE,"E30.top");var subQ1=sQuery(id+"F5.wireOp",EDGE,"E30.left");Q22=makeQuery(id+"F6.boolean.opBoolean","COPY",EDGE,{"disambiguationData":[TD([makeQuery(id+"F1.opExtrude","SWEPT_FACE",FACE,{"disambiguationData":[OSD([sQuery(id+"F0.wireOp",EDGE,"E0")])]})])],"derivedFrom":makeQuery(id+"F6.opExtrude","SWEPT_EDGE",EDGE,{"disambiguationData":[OSD([subQ0,subQ1])]})});}
            var Q23;
            {var subQ0=sQuery(id+"F5.wireOp",EDGE,"E31.left");var subQ1=sQuery(id+"F5.wireOp",EDGE,"E31.top");Q23=makeQuery(id+"F6.boolean.opBoolean","COPY",EDGE,{"disambiguationData":[TD([makeQuery(id+"F1.opExtrude","SWEPT_FACE",FACE,{"disambiguationData":[OSD([sQuery(id+"F0.wireOp",EDGE,"E0")])]})])],"derivedFrom":makeQuery(id+"F6.opExtrude","SWEPT_EDGE",EDGE,{"disambiguationData":[OSD([subQ1,subQ0])]})});}
            var Q24;
            {var subQ0=sQuery(id+"F5.wireOp",EDGE,"E28.bottom");var subQ1=sQuery(id+"F5.wireOp",EDGE,"E28.right");Q24=makeQuery(id+"F6.boolean.opBoolean","COPY",EDGE,{"disambiguationData":[TD([makeQuery(id+"F1.opExtrude","SWEPT_FACE",FACE,{"disambiguationData":[OSD([sQuery(id+"F0.wireOp",EDGE,"E0")])]})])],"derivedFrom":makeQuery(id+"F6.opExtrude","SWEPT_EDGE",EDGE,{"disambiguationData":[OSD([subQ0,subQ1])]})});}
            var Q25;
            {var subQ0=sQuery(id+"F5.wireOp",EDGE,"E29.top");var subQ1=sQuery(id+"F5.wireOp",EDGE,"E29.right");Q25=makeQuery(id+"F6.boolean.opBoolean","COPY",EDGE,{"disambiguationData":[TD([makeQuery(id+"F1.opExtrude","SWEPT_FACE",FACE,{"disambiguationData":[OSD([sQuery(id+"F0.wireOp",EDGE,"E0")])]})])],"derivedFrom":makeQuery(id+"F6.opExtrude","SWEPT_EDGE",EDGE,{"disambiguationData":[OSD([subQ0,subQ1])]})});}
            var Q26;
            {var subQ0=sQuery(id+"F5.wireOp",EDGE,"E30.right");var subQ1=sQuery(id+"F5.wireOp",EDGE,"E30.top");Q26=makeQuery(id+"F6.boolean.opBoolean","COPY",EDGE,{"disambiguationData":[TD([makeQuery(id+"F1.opExtrude","SWEPT_FACE",FACE,{"disambiguationData":[OSD([sQuery(id+"F0.wireOp",EDGE,"E0")])]})])],"derivedFrom":makeQuery(id+"F6.opExtrude","SWEPT_EDGE",EDGE,{"disambiguationData":[OSD([subQ1,subQ0])]})});}
            var Q27;
            {var subQ0=sQuery(id+"F5.wireOp",EDGE,"E31.top");var subQ1=sQuery(id+"F5.wireOp",EDGE,"E31.right");Q27=makeQuery(id+"F6.boolean.opBoolean","COPY",EDGE,{"disambiguationData":[TD([makeQuery(id+"F1.opExtrude","SWEPT_FACE",FACE,{"disambiguationData":[OSD([sQuery(id+"F0.wireOp",EDGE,"E0")])]})])],"derivedFrom":makeQuery(id+"F6.opExtrude","SWEPT_EDGE",EDGE,{"disambiguationData":[OSD([subQ0,subQ1])]})});}
            var Q28;
            {var subQ0=sQuery(id+"F5.wireOp",EDGE,"E28.top");var subQ1=sQuery(id+"F5.wireOp",EDGE,"E28.right");Q28=makeQuery(id+"F6.boolean.opBoolean","COPY",EDGE,{"disambiguationData":[TD([makeQuery(id+"F1.opExtrude","SWEPT_FACE",FACE,{"disambiguationData":[OSD([sQuery(id+"F0.wireOp",EDGE,"E0")])]})])],"derivedFrom":makeQuery(id+"F6.opExtrude","SWEPT_EDGE",EDGE,{"disambiguationData":[OSD([subQ0,subQ1])]})});}
            var Q29;
            {var subQ0=sQuery(id+"F5.wireOp",EDGE,"E29.bottom");var subQ1=sQuery(id+"F5.wireOp",EDGE,"E29.right");Q29=makeQuery(id+"F6.boolean.opBoolean","COPY",EDGE,{"disambiguationData":[TD([makeQuery(id+"F1.opExtrude","SWEPT_FACE",FACE,{"disambiguationData":[OSD([sQuery(id+"F0.wireOp",EDGE,"E0")])]})])],"derivedFrom":makeQuery(id+"F6.opExtrude","SWEPT_EDGE",EDGE,{"disambiguationData":[OSD([subQ0,subQ1])]})});}
            var Q30;
            {var subQ0=sQuery(id+"F5.wireOp",EDGE,"E30.bottom");var subQ1=sQuery(id+"F5.wireOp",EDGE,"E30.right");Q30=makeQuery(id+"F6.boolean.opBoolean","COPY",EDGE,{"disambiguationData":[TD([makeQuery(id+"F1.opExtrude","SWEPT_FACE",FACE,{"disambiguationData":[OSD([sQuery(id+"F0.wireOp",EDGE,"E0")])]})])],"derivedFrom":makeQuery(id+"F6.opExtrude","SWEPT_EDGE",EDGE,{"disambiguationData":[OSD([subQ0,subQ1])]})});}
            var Q31;
            {var subQ0=sQuery(id+"F5.wireOp",EDGE,"E31.bottom");var subQ1=sQuery(id+"F5.wireOp",EDGE,"E31.right");Q31=makeQuery(id+"F6.boolean.opBoolean","COPY",EDGE,{"disambiguationData":[TD([makeQuery(id+"F1.opExtrude","SWEPT_FACE",FACE,{"disambiguationData":[OSD([sQuery(id+"F0.wireOp",EDGE,"E0")])]})])],"derivedFrom":makeQuery(id+"F6.opExtrude","SWEPT_EDGE",EDGE,{"disambiguationData":[OSD([subQ0,subQ1])]})});}
            fillet(context, id + "F7", {"entities" : qUnion([Q0, Q1, Q2, Q3, Q4, Q5, Q6, Q7, Q8, Q9, Q10, Q11, Q12, Q13, Q14, Q15, Q16, Q17, Q18, Q19, Q20, Q21, Q22, Q23, Q24, Q25, Q26, Q27, Q28, Q29, Q30, Q31]), "radius" : 2 * mm, "tangentPropagation" : true, "allowEdgeOverflow" : false});
        }
        {
            var Q0;
            Q0=makeQuery(id+"F1.opExtrude","CAP_FACE",FACE,{"disambiguationData":[OSD([sQuery(id+"F0.wireOp",EDGE,"E0"),sQuery(id+"F0.wireOp",EDGE,"E1"),sQuery(id+"F0.wireOp",EDGE,"E2"),sQuery(id+"F0.wireOp",EDGE,"E4.filletArc"),sQuery(id+"F0.wireOp",EDGE,"E5.filletArc"),sQuery(id+"F0.wireOp",EDGE,"E6.0"),sQuery(id+"F0.wireOp",EDGE,"E7.0"),sQuery(id+"F0.wireOp",EDGE,"E8.0"),sQuery(id+"F0.wireOp",EDGE,"E8.1"),sQuery(id+"F0.wireOp",EDGE,"E8.2"),sQuery(id+"F0.wireOp",EDGE,"E9"),sQuery(id+"F0.wireOp",EDGE,"E10")])],"isStart":false});
            var sketch = newSketch(context, id + "F8", { "sketchPlane" : qUnion([Q0])});
            skLineSegment(sketch, "E37.0.0", {"start": v(60, 0) * mm, "end": v(60, -51) * mm, "construction": true});
            skArc(sketch, "E37.0.1", {"start": v(60, -51) * mm, "mid": v(57.36, -57.36) * mm, "end": v(51, -60) * mm, "construction": true});
            skLineSegment(sketch, "E37.0.2", {"start": v(51, -60) * mm, "end": v(-51, -60) * mm, "construction": true});
            skArc(sketch, "E37.0.3", {"start": v(-51, -60) * mm, "mid": v(-57.36, -57.36) * mm, "end": v(-60, -51) * mm, "construction": true});
            skLineSegment(sketch, "E37.0.4", {"start": v(-60, -51) * mm, "end": v(-60, 0) * mm, "construction": true});
            skLineSegment(sketch, "E37.0.5", {"start": v(-63, 0) * mm, "end": v(-66, 0) * mm});
            skLineSegment(sketch, "E37.0.6", {"start": v(-66, 0) * mm, "end": v(-66, -51) * mm});
            skArc(sketch, "E37.0.7", {"start": v(-66, -51) * mm, "mid": v(-61.6, -61.6) * mm, "end": v(-51, -66) * mm});
            skLineSegment(sketch, "E37.0.8", {"start": v(-51, -66) * mm, "end": v(51, -66) * mm});
            skArc(sketch, "E37.0.9", {"start": v(51, -66) * mm, "mid": v(61.6, -61.6) * mm, "end": v(66, -51) * mm});
            skLineSegment(sketch, "E37.0.10", {"start": v(66, -51) * mm, "end": v(66, 0) * mm});
            skLineSegment(sketch, "E37.0.11", {"start": v(66, 0) * mm, "end": v(63, 0) * mm});
            skLineSegment(sketch, "E38.0", {"start": v(-63, -51) * mm, "end": v(-63, 0) * mm});
            skArc(sketch, "E39.0", {"start": v(-51, -63) * mm, "mid": v(-59.49, -59.49) * mm, "end": v(-63, -51) * mm});
            skLineSegment(sketch, "E39.1", {"start": v(51, -63) * mm, "end": v(-51, -63) * mm});
            skArc(sketch, "E39.2", {"start": v(63, -51) * mm, "mid": v(59.49, -59.49) * mm, "end": v(51, -63) * mm});
            skLineSegment(sketch, "E39.3", {"start": v(63, 0) * mm, "end": v(63, -51) * mm});
            skSolve(sketch);
        }
        {
            var Q0;
            Q0 = qSketchRegion(id + "F8", true);
            extrude(context, id + "F9", {"entities" : qUnion([Q0]), "operationType" : NewBodyOperationType.REMOVE, "oppositeDirection" : true, "depth" : 7.5 * mm, "offsetDistance" : 25 * mm});
        }
    });
